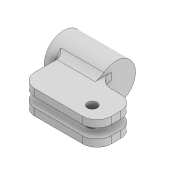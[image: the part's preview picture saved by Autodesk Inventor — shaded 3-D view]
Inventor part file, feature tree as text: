
AUTODESK INVENTOR PART (.ipt)
format: ipt  version: 2022 (Build 260153000, 153)  size: 198,144 bytes
history: native  units: mm
features: extrude x6, sketch x6, fillet x3, projected_geometry x2, mirror x1
ambient origin geometry x8: Origin, YZ Plane, XZ Plane, XY Plane, X Axis, Y Axis, Z Axis, Center Point
bodies: Solid1 (feature_tree)
feature tree (18):
  extrude  "Extrusion1"  Depth=12.2mm
  extrude  "Extrusion2"  Depth=20.0mm TaperAngle=0.0deg
  sketch  "Sketch6"  dims[d5=2.0mm d6=0.0mm d57=2.0mm]
  extrude  "Extrusion9"  Depth=2.0mm
  extrude  "Extrusion10"  Depth=32.0mm
  fillet  "Fillet5"  Radius=32.0mm
  fillet  "Fillet6"  Radius=4.1mm
  mirror  "Mirror1"
  extrude  "Extrusion11"  Depth=6.0mm
  extrude  "Extrusion12"  Depth=6.0mm
  fillet  "Fillet7"  Radius=2.0mm
  sketch  "Sketch1"  dims[d0=9.8mm d1=12.2mm]
  sketch  "Sketch2"  dims[d2=2.0mm d3=20.0mm d4=0.0mm]
  projected_geometry  "Projected Loop1"
  projected_geometry  "Projected Loop2"
  sketch  "Sketch11"  dims[d58=3.0mm d60=24.0mm d61=32.0mm d62=0.0mm d63=4.1mm]
  sketch  "Sketch12"  dims[d64=8.0mm d65=6.0mm]
  sketch  "Sketch14"  dims[d66=32.0mm d67=0.0mm d68=6.0mm d69=2.0mm d70=16.2mm d71=16.2mm d72=100.0mm d73=0.0mm d74=100.0mm d75=0.0mm d76=6.0mm]
